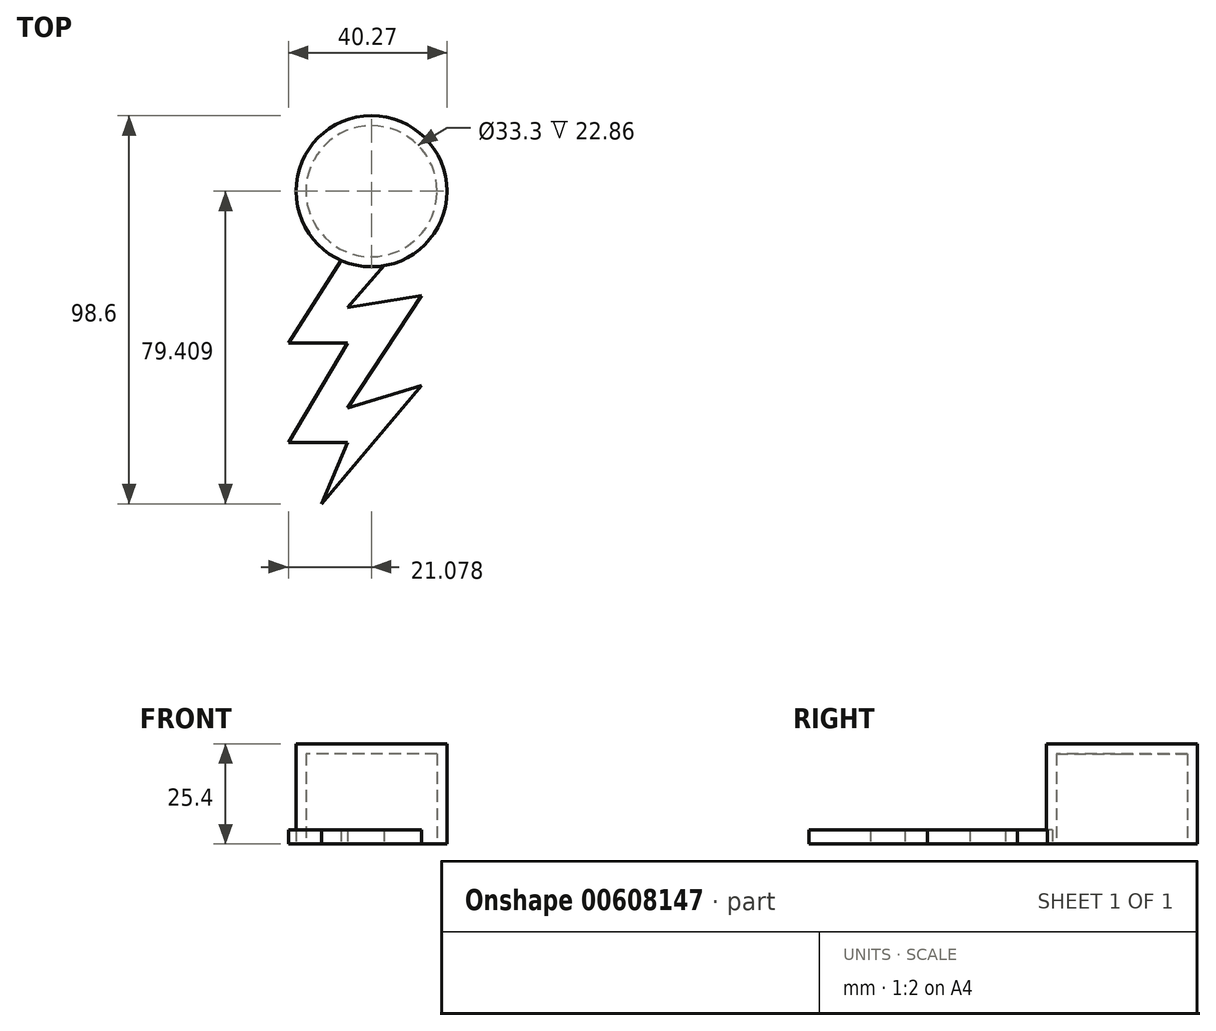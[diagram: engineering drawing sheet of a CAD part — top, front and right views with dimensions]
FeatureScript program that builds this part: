
annotation { "Feature Type Name" : "Feature", "Feature Type Description" : "" }
export const myFeature = defineFeature(function(context is Context, id is Id, definition is map)
    precondition{}
    {
        {
            var Q0;
            Q0=qCreatedBy(makeId("Top.planeOp"),FACE);
            var sketch = newSketch(context, id + "F0", { "sketchPlane" : qUnion([Q0])});
            skCircle(sketch, "E0", {"center": v(-22.32, 32.27) * mm, "radius": 19.19 * mm});
            skLineSegment(sketch, "E1", {"start": v(-30.05, 14.7) * mm, "end": v(-43.4, -6.29) * mm});
            skLineSegment(sketch, "E2", {"start": v(-43.4, -6.29) * mm, "end": v(-28.4, -6.29) * mm});
            skLineSegment(sketch, "E3", {"start": v(-28.4, -6.29) * mm, "end": v(-43.4, -31.52) * mm});
            skLineSegment(sketch, "E4", {"start": v(-43.4, -31.52) * mm, "end": v(-28.4, -31.52) * mm});
            skLineSegment(sketch, "E5", {"start": v(-28.4, -31.52) * mm, "end": v(-35, -47.14) * mm});
            skLineSegment(sketch, "E6", {"start": v(-35, -47.14) * mm, "end": v(-9.58, -17.1) * mm});
            skLineSegment(sketch, "E7", {"start": v(-9.58, -17.1) * mm, "end": v(-28.4, -22.8) * mm});
            skLineSegment(sketch, "E8", {"start": v(-28.4, -22.8) * mm, "end": v(-9.58, 5.75) * mm});
            skLineSegment(sketch, "E9", {"start": v(-9.58, 5.75) * mm, "end": v(-28.4, 2.67) * mm});
            skLineSegment(sketch, "E10", {"start": v(-28.4, 2.67) * mm, "end": v(-19.08, 13.35) * mm});
            skSolve(sketch);
        }
        {
            var Q0;
            {var subQ0=sQuery(id+"F0.wireOp",EDGE,"E0");var subQ1=makeQuery(id+"F0.imprint","INTERSECT",VERTEX,{"derivedFrom":[subQ0,sQuery(id+"F0.wireOp",EDGE,"E1")]});Q0=makeQuery(id+"F0.imprint","IMPRINT",FACE,{"disambiguationData":[TD([[makeQuery(id+"F0.imprint","IMPRINT",EDGE,{"disambiguationData":[TD([[subQ1,-1.0]])],"derivedFrom":subQ0}),1.0]])]});}
            var Q1;
            Q1=sQuery(id+"F0.wireOp",EDGE,"E0");
            extrude(context, id + "F1", {"entities" : qUnion([Q0]), "surfaceEntities" : qUnion([Q1]), "depth" : 25.4 * mm, "offsetDistance" : 25.4 * mm});
        }
        {
            var Q0;
            {var subQ0=sQuery(id+"F0.wireOp",EDGE,"E1");Q0=makeQuery(id+"F0.imprint","IMPRINT",FACE,{"disambiguationData":[TD([[makeQuery(id+"F0.imprint","IMPRINT",EDGE,{"derivedFrom":subQ0}),1.0]])]});}
            extrude(context, id + "F2", {"entities" : qUnion([Q0]), "depth" : 3.56 * mm, "offsetDistance" : 25.4 * mm});
        }
        {
            var Q0;
            Q0=makeQuery(id+"F1.opExtrude","CAP_FACE",FACE,{"disambiguationData":[OSD([sQuery(id+"F0.wireOp",EDGE,"E0")])],"isStart":true});
            shell(context, id + "F3", {"entities" : qUnion([Q0]), "thickness" : 2.54 * mm});
        }
    });
